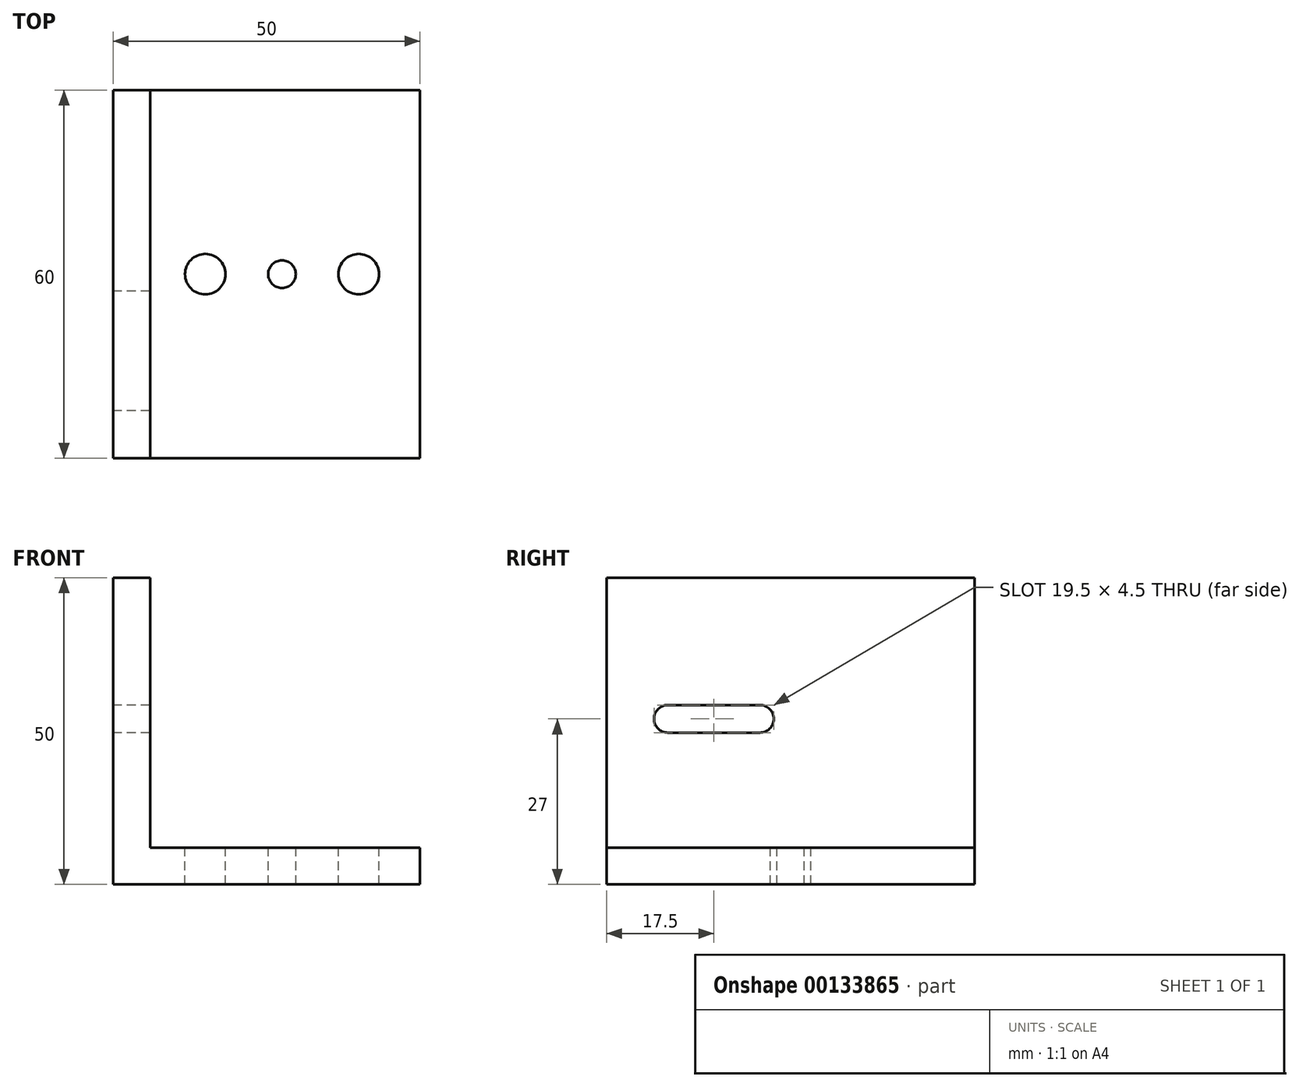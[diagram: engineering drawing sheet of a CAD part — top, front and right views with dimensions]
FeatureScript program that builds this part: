
annotation { "Feature Type Name" : "Feature", "Feature Type Description" : "" }
export const myFeature = defineFeature(function(context is Context, id is Id, definition is map)
    precondition{}
    {
        {
            var Q0;
            Q0=qCreatedBy(makeId("Top.planeOp"),FACE);
            var sketch = newSketch(context, id + "F0", { "sketchPlane" : qUnion([Q0])});
            skLineSegment(sketch, "E0.bottom", {"start": v(50, 0) * mm, "end": v(0, 0) * mm});
            skLineSegment(sketch, "E0.top", {"start": v(50, -60) * mm, "end": v(0, -60) * mm});
            skLineSegment(sketch, "E0.left", {"start": v(50, 0) * mm, "end": v(50, -60) * mm});
            skLineSegment(sketch, "E0.right", {"start": v(0, 0) * mm, "end": v(0, -60) * mm});
            skSolve(sketch);
        }
        {
            var Q0;
            Q0 = qSketchRegion(id + "F0", true);
            extrude(context, id + "F1", {"entities" : qUnion([Q0]), "depth" : 6 * mm});
        }
        {
            var Q0;
            Q0=makeQuery(id+"F1.opExtrude","CAP_FACE",FACE,{"disambiguationData":[OSD([sQuery(id+"F0.wireOp",EDGE,"E0.bottom"),sQuery(id+"F0.wireOp",EDGE,"E0.top"),sQuery(id+"F0.wireOp",EDGE,"E0.left"),sQuery(id+"F0.wireOp",EDGE,"E0.right")])],"isStart":false});
            var sketch = newSketch(context, id + "F2", { "sketchPlane" : qUnion([Q0])});
            skLineSegment(sketch, "E1.bottom", {"start": v(0, -60) * mm, "end": v(6, -60) * mm});
            skLineSegment(sketch, "E1.top", {"start": v(0, 0) * mm, "end": v(6, 0) * mm});
            skLineSegment(sketch, "E1.left", {"start": v(0, -60) * mm, "end": v(0, 0) * mm});
            skLineSegment(sketch, "E1.right", {"start": v(6, -60) * mm, "end": v(6, 0) * mm});
            skSolve(sketch);
        }
        {
            var Q0;
            Q0 = qSketchRegion(id + "F2", true);
            extrude(context, id + "F3", {"entities" : qUnion([Q0]), "operationType" : NewBodyOperationType.ADD, "depth" : 44 * mm});
        }
        {
            var Q0;
            Q0=makeQuery(id+"F3.opExtrude","SWEPT_FACE",FACE,{"disambiguationData":[OSD([sQuery(id+"F2.wireOp",EDGE,"E1.left")])]});
            var sketch = newSketch(context, id + "F4", { "sketchPlane" : qUnion([Q0])});
            skArc(sketch, "E2", {"start": v(35, 29.25) * mm, "mid": v(32.75, 27) * mm, "end": v(35, 24.75) * mm});
            skArc(sketch, "E3", {"start": v(50, 24.75) * mm, "mid": v(52.25, 27) * mm, "end": v(50, 29.25) * mm});
            skLineSegment(sketch, "E4", {"start": v(35, 29.25) * mm, "end": v(50, 29.25) * mm});
            skLineSegment(sketch, "E5", {"start": v(35, 24.75) * mm, "end": v(50, 24.75) * mm});
            skSolve(sketch);
        }
        {
            var Q0;
            Q0=makeQuery(id+"F4.imprint","IMPRINT",FACE,{"disambiguationData":[TD([[makeQuery(id+"F4.imprint","IMPRINT",EDGE,{"derivedFrom":sQuery(id+"F4.wireOp",EDGE,"E2")}),1.0]])]});
            var Q1;
            Q1 = qSketchRegion(id + "F4", true);
            extrude(context, id + "F5", {"entities" : qUnion([Q0, Q1]), "operationType" : NewBodyOperationType.REMOVE, "endBound" : BoundingType.THROUGH_ALL, "oppositeDirection" : true, "depth" : 25 * mm});
        }
        {
            var Q0;
            Q0=makeQuery(id+"F1.opExtrude","CAP_FACE",FACE,{"disambiguationData":[OSD([sQuery(id+"F0.wireOp",EDGE,"E0.bottom"),sQuery(id+"F0.wireOp",EDGE,"E0.top"),sQuery(id+"F0.wireOp",EDGE,"E0.left"),sQuery(id+"F0.wireOp",EDGE,"E0.right")])],"isStart":false});
            var sketch = newSketch(context, id + "F6", { "sketchPlane" : qUnion([Q0])});
            skCircle(sketch, "E6", {"center": v(15, -30) * mm, "radius": 3.3 * mm});
            skCircle(sketch, "E7", {"center": v(40, -30) * mm, "radius": 3.3 * mm});
            skCircle(sketch, "E8", {"center": v(27.5, -30) * mm, "radius": 2.25 * mm});
            skLineSegment(sketch, "E9", {"start": v(15, -30) * mm, "end": v(40, -30) * mm, "construction": true});
            skLineSegment(sketch, "E10", {"start": v(40, -30) * mm, "end": v(40, -60) * mm, "construction": true});
            skLineSegment(sketch, "E11", {"start": v(40, -30) * mm, "end": v(40, 0) * mm, "construction": true});
            skSolve(sketch);
        }
        {
            var Q0;
            Q0=makeQuery(id+"F6.imprint","IMPRINT",FACE,{"disambiguationData":[TD([[makeQuery(id+"F6.imprint","IMPRINT",EDGE,{"derivedFrom":sQuery(id+"F6.wireOp",EDGE,"E8")}),1.0]])]});
            var Q1;
            Q1 = qSketchRegion(id + "F6", true);
            var Q2;
            Q2=makeQuery(id+"F6.imprint","IMPRINT",FACE,{"disambiguationData":[TD([[makeQuery(id+"F6.imprint","IMPRINT",EDGE,{"derivedFrom":sQuery(id+"F6.wireOp",EDGE,"E7")}),1.0]])]});
            var Q3;
            Q3=makeQuery(id+"F6.imprint","IMPRINT",FACE,{"disambiguationData":[TD([[makeQuery(id+"F6.imprint","IMPRINT",EDGE,{"derivedFrom":sQuery(id+"F6.wireOp",EDGE,"E6")}),1.0]])]});
            extrude(context, id + "F7", {"entities" : qUnion([Q0, Q1, Q2, Q3]), "operationType" : NewBodyOperationType.REMOVE, "oppositeDirection" : true, "depth" : 25 * mm});
        }
    });
